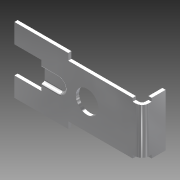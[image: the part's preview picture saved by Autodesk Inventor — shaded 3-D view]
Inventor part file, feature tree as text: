
AUTODESK INVENTOR PART (.ipt)
format: ipt  version: 2011 (Build 150239000, 239)  size: 228,864 bytes
history: native  units: mm (DEFAULTED — no unit token found)
features: sketch x9, other x7, sheet_metal_op x5, extrude x2, fillet x2, mirror x1
ambient origin geometry x8: Origin, YZ Plane, XZ Plane, XY Plane, X Axis, Y Axis, Z Axis, Center Point
bodies: Solid1 (feature_tree)
feature tree (26):
  sheet_metal_op  "Face1"
  sheet_metal_op  "Flange1"
  mirror  "Mirror1"
  extrude  "Extrusion1"  Depth=12.3952mm
  extrude  "Extrusion2"  Depth=0.762mm
  fillet  "Fillet3"  Radius=0.381mm
  fillet  "Fillet4"  Radius=1.524mm
  sheet_metal_op  "Face2"
  sketch  "Sketch1"  dims[d0=30.1752mm d1=12.3952mm]
  other  "Plate1"
  sketch  "Sketch2"  dims[d2=0.762mm d3=0.762mm d4=0.381mm d5=1.524mm]
  other  "Plate2"
  sheet_metal_op  "Bend1"
  sketch  "Sketch3"  dims[d6=0.762mm]
  sketch  "Sketch4"  dims[d7=4.7752mm d8=90.0deg d9=0.762mm]
  sketch  "Sketch5"  dims[d10=1.5748mm]
  sketch  "Sketch6"  dims[d11=1.5748mm]
  sketch  "Sketch8"  dims[d12=0.7874mm]
  sketch  "Sketch9"  dims[d13=0.762mm]
  sketch  "Sketch11"  dims[d14=0.0mm d15=6.35mm d16=6.35mm d17=0.762mm d18=0.0mm d19=5.334mm d20=13.0048mm d21=0.762mm d22=0.0mm d23=4.7752mm d24=3.9624mm d25=0.762mm d26=0.0mm d29=0.762mm d30=0.762mm d31=0.0mm d32=0.381mm d33=0.381mm d34=1.524mm d35=3.175mm d36=0.762mm d37=0.0mm d39=1.5748mm d40=12.7mm d41=0.762mm d42=0.762mm d43=0.381mm d44=1.524mm d45=0.762mm d46=12.7mm d47=1.5748mm]
  other  "Plate3"
  sheet_metal_op  "Bend2"
  other  "Cut1"
  other  "Cut2"
  other  "Cut3"
  other  "Cut4"
